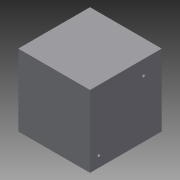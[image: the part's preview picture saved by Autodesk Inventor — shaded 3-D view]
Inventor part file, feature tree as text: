
AUTODESK INVENTOR PART (.ipt)
format: ipt  version: 2014 (Build 180170000, 170)  size: 148,480 bytes
history: native  units: mm
features: other x48, extrude x5, sketch x5
ambient origin geometry x8: Origin, YZ Plane, XZ Plane, XY Plane, X Axis, Y Axis, Z Axis, Center Point
bodies: 实体1 (feature_tree)
feature tree (58):
  extrude  "拉伸1"  Depth=32.0mm
  other  "UCS1"
  other  "UCS2"
  other  "UCS3"
  other  "UCS4"
  other  "UCS5"
  other  "UCS6"
  extrude  "拉伸2"  Depth=32.0mm
  extrude  "拉伸3"  Depth=32.0mm
  extrude  "拉伸4"  Depth=32.0mm TaperAngle=0.0deg
  extrude  "拉伸5"  Depth=32.0mm
  sketch  "草图1"  dims[d0=400.0mm d1=0.0mm]
  sketch  "草图2"  dims[d2=0.0mm d3=0.0mm d4=0.0mm d5=0.0mm d6=0.0mm d7=0.0mm]
  sketch  "草图3"  dims[d8=0.0mm d9=0.0mm d10=0.0mm d11=0.0mm d12=0.0mm d13=0.0mm]
  sketch  "草图4"  dims[d14=0.0mm d15=0.0mm d16=0.0mm d17=0.0mm d18=0.0mm d19=0.0mm]
  sketch  "草图8"  dims[d20=0.0mm d21=0.0mm d22=0.0mm d23=0.0mm d24=0.0mm d25=0.0mm d26=0.0mm d27=0.0mm d28=0.0mm d29=0.0mm d30=0.0mm d31=0.0mm d32=0.0mm d33=0.0mm d34=0.0mm d35=0.0mm d36=0.0mm d37=0.0mm d38=50.0mm d39=60.0mm d42=14.0mm d43=44.0mm d44=0.0mm d45=44.0mm d46=-10.297443mm d47=44.0mm d48=-10.297443mm d64=16.0mm d65=32.0mm d66=0.0mm d132=100.0mm d133=80.0mm]
  other  "UCS1: YZ 平面"
  other  "UCS1: XZ 平面"
  other  "UCS1: XY 平面"
  other  "UCS1: X 轴"
  other  "UCS1: Y 轴"
  other  "UCS1: Z 轴"
  other  "UCS1: 原点"
  other  "UCS2: YZ 平面"
  other  "UCS2: XZ 平面"
  other  "UCS2: XY 平面"
  other  "UCS2: X 轴"
  other  "UCS2: Y 轴"
  other  "UCS2: Z 轴"
  other  "UCS2: 原点"
  other  "UCS3: YZ 平面"
  other  "UCS3: XZ 平面"
  other  "UCS3: XY 平面"
  other  "UCS3: X 轴"
  other  "UCS3: Y 轴"
  other  "UCS3: Z 轴"
  other  "UCS3: 原点"
  other  "UCS4: YZ 平面"
  other  "UCS4: XZ 平面"
  other  "UCS4: XY 平面"
  other  "UCS4: X 轴"
  other  "UCS4: Y 轴"
  other  "UCS4: Z 轴"
  other  "UCS4: 原点"
  other  "UCS5: YZ 平面"
  other  "UCS5: XZ 平面"
  other  "UCS5: XY 平面"
  other  "UCS5: X 轴"
  other  "UCS5: Y 轴"
  other  "UCS5: Z 轴"
  other  "UCS5: 原点"
  other  "UCS6: YZ 平面"
  other  "UCS6: XZ 平面"
  other  "UCS6: XY 平面"
  other  "UCS6: X 轴"
  other  "UCS6: Y 轴"
  other  "UCS6: Z 轴"
  other  "UCS6: 原点"
